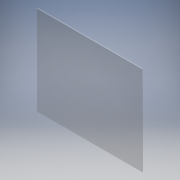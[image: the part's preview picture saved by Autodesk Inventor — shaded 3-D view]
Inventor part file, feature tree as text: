
AUTODESK INVENTOR PART (.ipt)
format: ipt  version: 2019.4 (Build 234330000, 330)  size: 105,472 bytes
history: native  units: mm
features: other x1, extrude x1, sketch x1
ambient origin geometry x8: Origin, YZ Plane, XZ Plane, XY Plane, X Axis, Y Axis, Z Axis, Center Point
bodies: Body1 (feature_tree)
feature tree (3):
  other  "Sólido1"
  extrude  "Extrusão1"  Depth=1200.0mm
  sketch  "Esboço1"  dims[d0=1020.0mm d1=1200.0mm d2=10.0mm d3=0.0mm]
